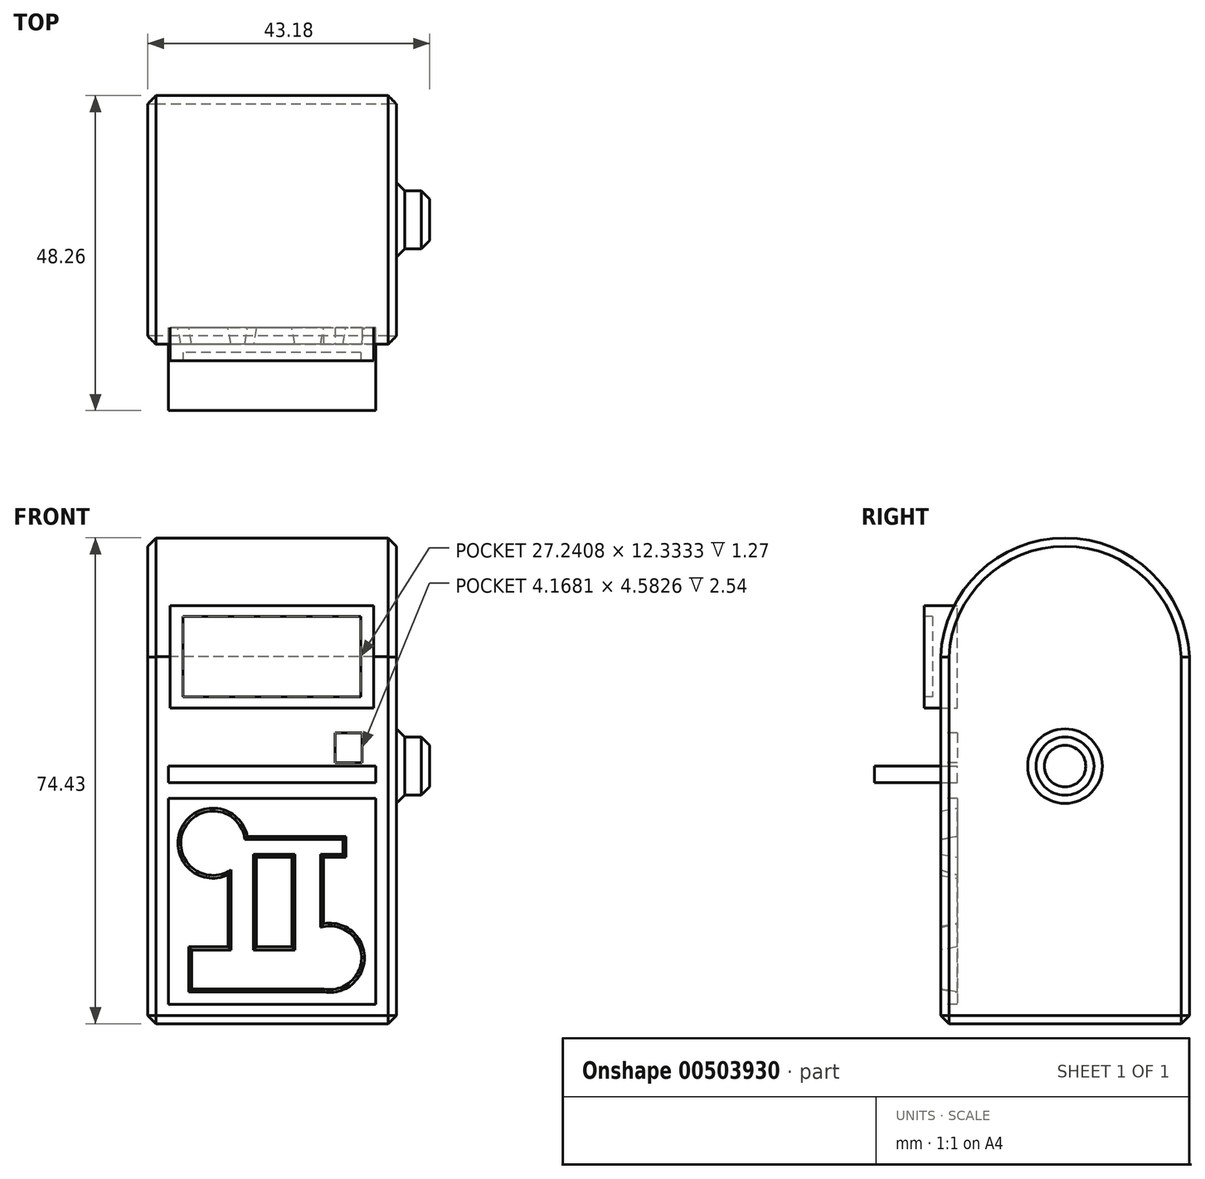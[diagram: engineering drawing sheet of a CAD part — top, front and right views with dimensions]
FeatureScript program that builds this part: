
annotation { "Feature Type Name" : "Feature", "Feature Type Description" : "" }
export const myFeature = defineFeature(function(context is Context, id is Id, definition is map)
    precondition{}
    {
        {
            var Q0;
            Q0=qCreatedBy(makeId("Top.planeOp"),FACE);
            var sketch = newSketch(context, id + "F0", { "sketchPlane" : qUnion([Q0])});
            skLineSegment(sketch, "E0.bottom", {"start": v(19.05, 19.05) * mm, "end": v(-19.05, 19.05) * mm});
            skLineSegment(sketch, "E0.top", {"start": v(19.05, -19.05) * mm, "end": v(-19.05, -19.05) * mm});
            skLineSegment(sketch, "E0.left", {"start": v(19.05, 19.05) * mm, "end": v(19.05, -19.05) * mm});
            skLineSegment(sketch, "E0.right", {"start": v(-19.05, 19.05) * mm, "end": v(-19.05, -19.05) * mm});
            skPoint(sketch, "E0.middle", {"position": v(0, 0) * mm});
            skSolve(sketch);
        }
        {
            var Q0;
            Q0=makeQuery(id+"F0.imprint","IMPRINT",FACE,{"disambiguationData":[TD([[makeQuery(id+"F0.imprint","IMPRINT",EDGE,{"derivedFrom":sQuery(id+"F0.wireOp",EDGE,"E0.bottom")}),1.0]])]});
            extrude(context, id + "F1", {"entities" : qUnion([Q0]), "depth" : 76.2 * mm});
        }
        {
            var Q0;
            Q0=makeQuery(id+"F1.opExtrude","SWEPT_FACE",FACE,{"disambiguationData":[OSD([sQuery(id+"F0.wireOp",EDGE,"E0.right")])]});
            var sketch = newSketch(context, id + "F2", { "sketchPlane" : qUnion([Q0])});
            skArc(sketch, "E1", {"start": v(19.05, 54.5) * mm, "mid": v(0.85, 74.4) * mm, "end": v(-19.05, 56.2) * mm});
            skLineSegment(sketch, "E2", {"start": v(-19.05, 56.2) * mm, "end": v(-19.05, 76.2) * mm});
            skLineSegment(sketch, "E3", {"start": v(-19.05, 76.2) * mm, "end": v(19.05, 76.2) * mm});
            skLineSegment(sketch, "E4", {"start": v(19.05, 76.2) * mm, "end": v(19.05, 54.5) * mm});
            skSolve(sketch);
        }
        {
            var Q0;
            {var subQ0=sQuery(id+"F2.wireOp",EDGE,"E2");Q0=makeQuery(id+"F2.imprint","IMPRINT",FACE,{"disambiguationData":[TD([[makeQuery(id+"F2.imprint","IMPRINT",EDGE,{"derivedFrom":subQ0}),1.0]])]});}
            extrude(context, id + "F3", {"entities" : qUnion([Q0]), "operationType" : NewBodyOperationType.REMOVE, "oppositeDirection" : true, "depth" : 41.4 * mm});
        }
        {
            var Q0;
            Q0=makeQuery(id+"F1.opExtrude","SWEPT_FACE",FACE,{"disambiguationData":[OSD([sQuery(id+"F0.wireOp",EDGE,"E0.left")])]});
            var sketch = newSketch(context, id + "F4", { "sketchPlane" : qUnion([Q0])});
            skCircle(sketch, "E5", {"center": v(0, 39.47) * mm, "radius": 4.44 * mm});
            skSolve(sketch);
        }
        {
            var Q0;
            Q0=makeQuery(id+"F4.imprint","IMPRINT",FACE,{"disambiguationData":[TD([[makeQuery(id+"F4.imprint","IMPRINT",EDGE,{"derivedFrom":sQuery(id+"F4.wireOp",EDGE,"E5")}),1.0]])]});
            extrude(context, id + "F5", {"entities" : qUnion([Q0]), "operationType" : NewBodyOperationType.ADD, "depth" : 5.08 * mm});
        }
        {
            var Q0;
            Q0=makeQuery(id+"F1.opExtrude","SWEPT_FACE",FACE,{"disambiguationData":[OSD([sQuery(id+"F0.wireOp",EDGE,"E0.right")])]});
            var Q1;
            Q1=makeQuery(id+"F1.opExtrude","SWEPT_FACE",FACE,{"disambiguationData":[OSD([sQuery(id+"F0.wireOp",EDGE,"E0.left")])]});
            var Q2;
            Q2=makeQuery(id+"F1.opExtrude","CAP_EDGE",EDGE,{"disambiguationData":[OSD([sQuery(id+"F0.wireOp",EDGE,"E0.top")])],"isStart":true});
            var Q3;
            Q3=makeQuery(id+"F1.opExtrude","CAP_EDGE",EDGE,{"disambiguationData":[OSD([sQuery(id+"F0.wireOp",EDGE,"E0.bottom")])],"isStart":true});
            var Q4;
            Q4=makeQuery(id+"F5.opExtrude","CAP_EDGE",EDGE,{"disambiguationData":[OSD([sQuery(id+"F4.wireOp",EDGE,"E5")])],"isStart":false});
            chamfer(context, id + "F6", {"entities" : qUnion([Q0, Q1, Q2, Q3, Q4]), "chamferType" : ChamferType.OFFSET_ANGLE, "width" : 1.27 * mm, "oppositeDirection" : false, "angle" : 45 * degree, "tangentPropagation" : true});
        }
        {
            var Q0;
            Q0=makeQuery(id+"F1.opExtrude","SWEPT_FACE",FACE,{"disambiguationData":[OSD([sQuery(id+"F0.wireOp",EDGE,"E0.top")])]});
            var sketch = newSketch(context, id + "F7", { "sketchPlane" : qUnion([Q0])});
            skLineSegment(sketch, "E6.bottom", {"start": v(-15.59, 48.37) * mm, "end": v(15.59, 48.37) * mm});
            skLineSegment(sketch, "E6.top", {"start": v(-15.59, 64.05) * mm, "end": v(15.59, 64.05) * mm});
            skLineSegment(sketch, "E6.left", {"start": v(-15.59, 48.37) * mm, "end": v(-15.59, 64.05) * mm});
            skLineSegment(sketch, "E6.right", {"start": v(15.59, 48.37) * mm, "end": v(15.59, 64.05) * mm});
            skPoint(sketch, "E6.middle", {"position": v(0, 56.2) * mm});
            skLineSegment(sketch, "E7.bottom", {"start": v(15.87, 36.91) * mm, "end": v(-15.87, 36.91) * mm});
            skLineSegment(sketch, "E7.top", {"start": v(15.87, 39.47) * mm, "end": v(-15.87, 39.47) * mm});
            skLineSegment(sketch, "E7.left", {"start": v(15.87, 36.91) * mm, "end": v(15.87, 39.47) * mm});
            skLineSegment(sketch, "E7.right", {"start": v(-15.87, 36.91) * mm, "end": v(-15.87, 39.47) * mm});
            skPoint(sketch, "E7.middle", {"position": v(0, 38.2) * mm});
            skLineSegment(sketch, "E8.bottom", {"start": v(13.82, 44.54) * mm, "end": v(9.65, 44.54) * mm});
            skLineSegment(sketch, "E8.top", {"start": v(13.82, 39.95) * mm, "end": v(9.65, 39.95) * mm});
            skLineSegment(sketch, "E8.left", {"start": v(13.82, 44.54) * mm, "end": v(13.82, 39.95) * mm});
            skLineSegment(sketch, "E8.right", {"start": v(9.65, 44.54) * mm, "end": v(9.65, 39.95) * mm});
            skPoint(sketch, "E8.middle", {"position": v(11.73, 42.25) * mm});
            skLineSegment(sketch, "E9.bottom", {"start": v(15.87, 34.54) * mm, "end": v(-15.87, 34.54) * mm});
            skLineSegment(sketch, "E9.top", {"start": v(15.87, 2.94) * mm, "end": v(-15.87, 2.94) * mm});
            skLineSegment(sketch, "E9.left", {"start": v(15.87, 34.54) * mm, "end": v(15.87, 2.94) * mm});
            skLineSegment(sketch, "E9.right", {"start": v(-15.87, 34.54) * mm, "end": v(-15.87, 2.94) * mm});
            skPoint(sketch, "E9.middle", {"position": v(0, 18.74) * mm});
            skSolve(sketch);
        }
        {
            var Q0;
            Q0=makeQuery(id+"F7.imprint","IMPRINT",FACE,{"disambiguationData":[TD([[makeQuery(id+"F7.imprint","IMPRINT",EDGE,{"derivedFrom":sQuery(id+"F7.wireOp",EDGE,"E9.bottom")}),1.0]])]});
            var Q1;
            Q1=makeQuery(id+"F7.imprint","IMPRINT",FACE,{"disambiguationData":[TD([[makeQuery(id+"F7.imprint","IMPRINT",EDGE,{"derivedFrom":sQuery(id+"F7.wireOp",EDGE,"E8.bottom")}),1.0]])]});
            extrude(context, id + "F8", {"entities" : qUnion([Q0, Q1]), "operationType" : NewBodyOperationType.REMOVE, "oppositeDirection" : true, "depth" : 2.54 * mm});
        }
        {
            var Q0;
            {var subQ0=sQuery(id+"F7.wireOp",EDGE,"E6.top");Q0=makeQuery(id+"F7.imprint","IMPRINT",FACE,{"disambiguationData":[TD([[makeQuery(id+"F7.imprint","IMPRINT",EDGE,{"derivedFrom":subQ0}),-1.0]])]});}
            var Q1;
            {var subQ0=sQuery(id+"F7.wireOp",EDGE,"E6.bottom");Q1=makeQuery(id+"F7.imprint","IMPRINT",FACE,{"disambiguationData":[TD([[makeQuery(id+"F7.imprint","IMPRINT",EDGE,{"derivedFrom":subQ0}),1.0]])]});}
            var Q2;
            Q2=makeQuery(id+"F7.imprint","IMPRINT",FACE,{"disambiguationData":[TD([[makeQuery(id+"F7.imprint","IMPRINT",EDGE,{"derivedFrom":sQuery(id+"F7.wireOp",EDGE,"E7.bottom")}),-1.0]])]});
            extrude(context, id + "F9", {"entities" : qUnion([Q0, Q1, Q2]), "depth" : 2.54 * mm, "hasSecondDirection" : true, "secondDirectionOppositeDirection" : true, "secondDirectionDepth" : 2.54 * mm});
        }
        {
            var Q0;
            Q0=makeQuery(id+"F9.opExtrude","CAP_FACE",FACE,{"disambiguationData":[OSD([sQuery(id+"F7.wireOp",EDGE,"E6.bottom"),sQuery(id+"F7.wireOp",EDGE,"E6.top"),sQuery(id+"F7.wireOp",EDGE,"E6.left"),sQuery(id+"F7.wireOp",EDGE,"E6.right")])],"isStart":false});
            var sketch = newSketch(context, id + "F10", { "sketchPlane" : qUnion([Q0])});
            skLineSegment(sketch, "E10.bottom", {"start": v(13.62, 62.42) * mm, "end": v(-13.62, 62.42) * mm});
            skLineSegment(sketch, "E10.top", {"start": v(13.62, 50.09) * mm, "end": v(-13.62, 50.09) * mm});
            skLineSegment(sketch, "E10.left", {"start": v(13.62, 62.42) * mm, "end": v(13.62, 50.09) * mm});
            skLineSegment(sketch, "E10.right", {"start": v(-13.62, 62.42) * mm, "end": v(-13.62, 50.09) * mm});
            skPoint(sketch, "E10.middle", {"position": v(0, 56.26) * mm});
            skSolve(sketch);
        }
        {
            var Q0;
            Q0=makeQuery(id+"F10.imprint","IMPRINT",FACE,{"disambiguationData":[TD([[makeQuery(id+"F10.imprint","IMPRINT",EDGE,{"derivedFrom":sQuery(id+"F10.wireOp",EDGE,"E10.bottom")}),1.0]])]});
            extrude(context, id + "F11", {"entities" : qUnion([Q0]), "operationType" : NewBodyOperationType.REMOVE, "oppositeDirection" : true, "depth" : 1.27 * mm});
        }
        {
            var Q0;
            Q0=makeQuery(id+"F9.opExtrude","CAP_FACE",FACE,{"disambiguationData":[OSD([sQuery(id+"F7.wireOp",EDGE,"E7.bottom"),sQuery(id+"F7.wireOp",EDGE,"E7.top"),sQuery(id+"F7.wireOp",EDGE,"E7.left"),sQuery(id+"F7.wireOp",EDGE,"E7.right")])],"isStart":false});
            extrude(context, id + "F12", {"entities" : qUnion([Q0]), "operationType" : NewBodyOperationType.ADD, "depth" : 7.62 * mm});
        }
        {
            var Q0;
            Q0=makeQuery(id+"F8.boolean.opBoolean","COPY",FACE,{"derivedFrom":makeQuery(id+"F8.opExtrude","CAP_FACE",FACE,{"disambiguationData":[OSD([sQuery(id+"F7.wireOp",EDGE,"E9.bottom"),sQuery(id+"F7.wireOp",EDGE,"E9.top"),sQuery(id+"F7.wireOp",EDGE,"E9.left"),sQuery(id+"F7.wireOp",EDGE,"E9.right")])],"isStart":false})});
            var sketch = newSketch(context, id + "F13", { "sketchPlane" : qUnion([Q0])});
            skCircle(sketch, "E11", {"center": v(-9.05, 27.65) * mm, "radius": 5.37 * mm});
            skLineSegment(sketch, "E12.bottom", {"start": v(11.32, 28.7) * mm, "end": v(-11.32, 28.7) * mm});
            skLineSegment(sketch, "E12.top", {"start": v(11.32, 25.5) * mm, "end": v(-11.32, 25.5) * mm});
            skLineSegment(sketch, "E12.left", {"start": v(11.32, 28.7) * mm, "end": v(11.32, 25.5) * mm});
            skLineSegment(sketch, "E12.right", {"start": v(-11.32, 28.7) * mm, "end": v(-11.32, 25.5) * mm});
            skPoint(sketch, "E12.middle", {"position": v(0, 27.1) * mm});
            skLineSegment(sketch, "E13.bottom", {"start": v(-2.4, 25.5) * mm, "end": v(-6.74, 25.5) * mm});
            skLineSegment(sketch, "E13.top", {"start": v(-2.4, 10.08) * mm, "end": v(-6.74, 10.08) * mm});
            skLineSegment(sketch, "E13.left", {"start": v(-2.4, 25.5) * mm, "end": v(-2.4, 10.08) * mm});
            skLineSegment(sketch, "E13.right", {"start": v(-6.74, 25.5) * mm, "end": v(-6.74, 10.08) * mm});
            skPoint(sketch, "E13.middle", {"position": v(-4.57, 17.8) * mm});
            skLineSegment(sketch, "E14.bottom", {"start": v(7.9, 25.5) * mm, "end": v(3.03, 25.5) * mm});
            skLineSegment(sketch, "E14.top", {"start": v(7.9, 4.88) * mm, "end": v(3.03, 4.88) * mm});
            skLineSegment(sketch, "E14.left", {"start": v(7.9, 25.5) * mm, "end": v(7.9, 4.88) * mm});
            skLineSegment(sketch, "E14.right", {"start": v(3.03, 25.5) * mm, "end": v(3.03, 4.88) * mm});
            skPoint(sketch, "E14.middle", {"position": v(5.47, 15.2) * mm});
            skLineSegment(sketch, "E15.bottom", {"start": v(3.03, 11.76) * mm, "end": v(-12.74, 11.76) * mm});
            skLineSegment(sketch, "E15.top", {"start": v(3.03, 4.88) * mm, "end": v(-12.74, 4.88) * mm});
            skLineSegment(sketch, "E15.left", {"start": v(3.03, 11.76) * mm, "end": v(3.03, 4.88) * mm});
            skLineSegment(sketch, "E15.right", {"start": v(-12.74, 11.76) * mm, "end": v(-12.74, 4.88) * mm});
            skPoint(sketch, "E15.middle", {"position": v(-4.85, 8.32) * mm});
            skCircle(sketch, "E16", {"center": v(8.85, 10.1) * mm, "radius": 5.3 * mm});
            skSolve(sketch);
        }
        {
            var Q0;
            Q0 = qSketchRegion(id + "F13", true);
            extrude(context, id + "F14", {"entities" : qUnion([Q0]), "operationType" : NewBodyOperationType.ADD, "depth" : 2.54 * mm, "hasDraft" : true, "draftAngle" : 10 * degree, "draftPullDirection" : true});
        }
    });
